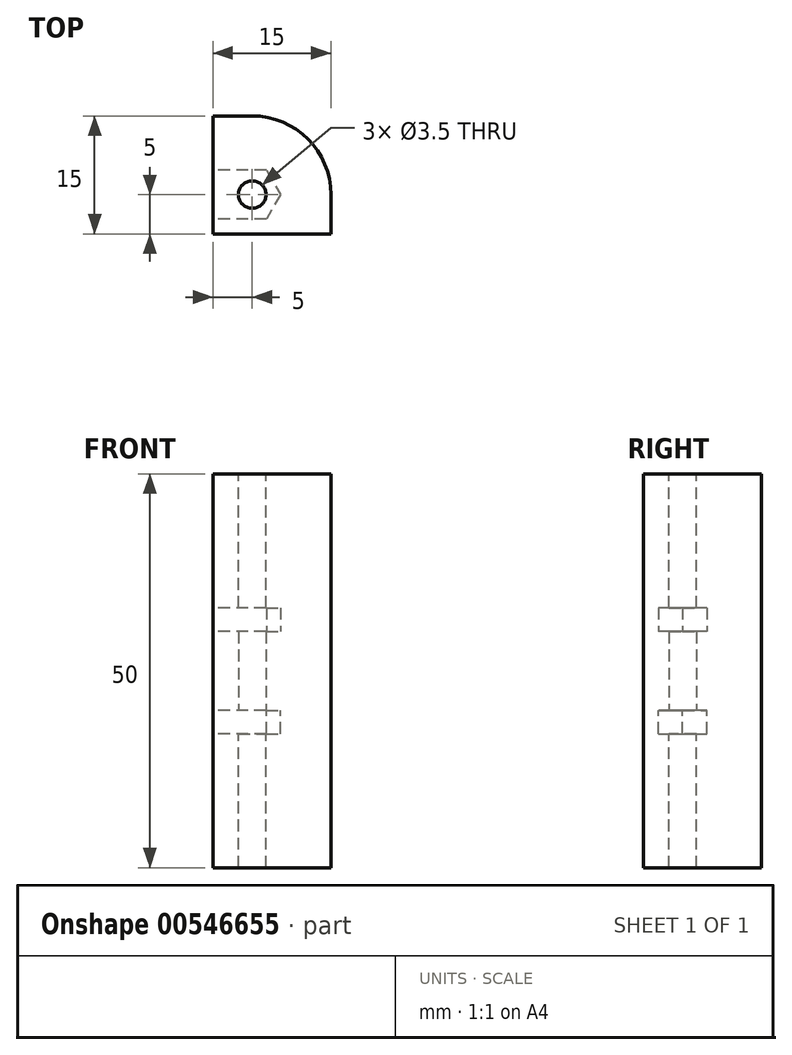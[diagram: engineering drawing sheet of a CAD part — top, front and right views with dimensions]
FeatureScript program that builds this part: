
annotation { "Feature Type Name" : "Feature", "Feature Type Description" : "" }
export const myFeature = defineFeature(function(context is Context, id is Id, definition is map)
    precondition{}
    {
        {
            var Q0;
            Q0=qCreatedBy(makeId("Top.planeOp"),FACE);
            var sketch = newSketch(context, id + "F0", { "sketchPlane" : qUnion([Q0])});
            skLineSegment(sketch, "E0.bottom", {"start": v(-2.5, 7.5) * mm, "end": v(-7.5, 7.5) * mm});
            skLineSegment(sketch, "E0.top", {"start": v(7.5, -7.5) * mm, "end": v(-7.5, -7.5) * mm});
            skLineSegment(sketch, "E0.left", {"start": v(7.5, -2.5) * mm, "end": v(7.5, -7.5) * mm});
            skLineSegment(sketch, "E0.right", {"start": v(-7.5, 7.5) * mm, "end": v(-7.5, -7.5) * mm});
            skPoint(sketch, "E0.middle", {"position": v(0, 0) * mm});
            skPoint(sketch, "E1.visualSharp", {"position": v(7.5, 7.5) * mm});
            skArc(sketch, "E1.filletArc", {"start": v(7.5, -2.5) * mm, "mid": v(4.57, 4.57) * mm, "end": v(-2.5, 7.5) * mm});
            skCircle(sketch, "E2", {"center": v(-2.5, -2.5) * mm, "radius": 1.75 * mm});
            skSolve(sketch);
        }
        {
            var Q0;
            Q0=makeQuery(id+"F0.imprint","IMPRINT",FACE,{"disambiguationData":[TD([[makeQuery(id+"F0.imprint","IMPRINT",EDGE,{"derivedFrom":sQuery(id+"F0.wireOp",EDGE,"E0.bottom")}),1.0]])]});
            extrude(context, id + "F1", {"entities" : qUnion([Q0]), "endBound" : BoundingType.SYMMETRIC, "depth" : 10 * mm, "offsetDistance" : 25 * mm});
        }
        {
            var Q0;
            Q0=makeQuery(id+"F1.opExtrude","CAP_FACE",FACE,{"disambiguationData":[OSD([sQuery(id+"F0.wireOp",EDGE,"E0.bottom"),sQuery(id+"F0.wireOp",EDGE,"E0.top"),sQuery(id+"F0.wireOp",EDGE,"E0.left"),sQuery(id+"F0.wireOp",EDGE,"E0.right"),sQuery(id+"F0.wireOp",EDGE,"E1.filletArc"),sQuery(id+"F0.wireOp",EDGE,"E2")])],"isStart":false});
            var sketch = newSketch(context, id + "F2", { "sketchPlane" : qUnion([Q0])});
            skLineSegment(sketch, "E3.0", {"start": v(-4.29, 0.6) * mm, "end": v(-0.71, 0.6) * mm});
            skLineSegment(sketch, "E3.1", {"start": v(-0.71, 0.6) * mm, "end": v(1.08, -2.5) * mm});
            skLineSegment(sketch, "E3.2", {"start": v(1.08, -2.5) * mm, "end": v(-0.71, -5.6) * mm});
            skLineSegment(sketch, "E3.3", {"start": v(-0.71, -5.6) * mm, "end": v(-4.29, -5.6) * mm});
            skPoint(sketch, "E3.0.midPoint", {"position": v(-2.5, 0.6) * mm});
            skLineSegment(sketch, "E4", {"start": v(-4.29, 0.6) * mm, "end": v(-7.5, 0.6) * mm});
            skLineSegment(sketch, "E5", {"start": v(-4.29, -5.6) * mm, "end": v(-7.5, -5.6) * mm});
            skSolve(sketch);
        }
        {
            var Q0;
            Q0=makeQuery(id+"F2.imprint","IMPRINT",FACE,{"disambiguationData":[TD([[makeQuery(id+"F2.imprint","IMPRINT",EDGE,{"derivedFrom":sQuery(id+"F2.wireOp",EDGE,"E3.0")}),1.0]])]});
            extrude(context, id + "F3", {"entities" : qUnion([Q0]), "operationType" : NewBodyOperationType.ADD, "depth" : 3 * mm, "offsetDistance" : 25 * mm});
        }
        {
            var Q0;
            Q0=makeQuery(id+"F1.opExtrude","CAP_FACE",FACE,{"disambiguationData":[OSD([sQuery(id+"F0.wireOp",EDGE,"E0.bottom"),sQuery(id+"F0.wireOp",EDGE,"E0.top"),sQuery(id+"F0.wireOp",EDGE,"E0.left"),sQuery(id+"F0.wireOp",EDGE,"E0.right"),sQuery(id+"F0.wireOp",EDGE,"E1.filletArc"),sQuery(id+"F0.wireOp",EDGE,"E2")])],"isStart":true});
            var sketch = newSketch(context, id + "F4", { "sketchPlane" : qUnion([Q0])});
            skLineSegment(sketch, "E6.0", {"start": v(-0.71, -0.6) * mm, "end": v(-4.29, -0.6) * mm});
            skLineSegment(sketch, "E6.3", {"start": v(-4.29, 5.6) * mm, "end": v(-0.71, 5.6) * mm});
            skLineSegment(sketch, "E6.4", {"start": v(-0.71, 5.6) * mm, "end": v(1.08, 2.5) * mm});
            skLineSegment(sketch, "E6.5", {"start": v(1.08, 2.5) * mm, "end": v(-0.71, -0.6) * mm});
            skPoint(sketch, "E6.0.midPoint", {"position": v(-2.5, -0.6) * mm});
            skLineSegment(sketch, "E7", {"start": v(-4.29, 5.6) * mm, "end": v(-7.5, 5.6) * mm});
            skLineSegment(sketch, "E8", {"start": v(-4.29, -0.6) * mm, "end": v(-7.5, -0.6) * mm});
            skSolve(sketch);
        }
        {
            var Q0;
            Q0 = qSketchRegion(id + "F4", true);
            var Q1;
            Q1=makeQuery(id+"F4.imprint","IMPRINT",FACE,{"disambiguationData":[TD([[makeQuery(id+"F4.imprint","IMPRINT",EDGE,{"derivedFrom":sQuery(id+"F4.wireOp",EDGE,"E6.0")}),1.0]])]});
            extrude(context, id + "F5", {"entities" : qUnion([Q0, Q1]), "operationType" : NewBodyOperationType.ADD, "depth" : 3 * mm, "offsetDistance" : 25 * mm});
        }
        {
            var Q0;
            Q0=makeQuery(id+"F3.opExtrude","CAP_FACE",FACE,{"disambiguationData":[OSD([sQuery(id+"F0.wireOp",EDGE,"E0.bottom"),sQuery(id+"F0.wireOp",EDGE,"E0.top"),sQuery(id+"F0.wireOp",EDGE,"E0.left"),sQuery(id+"F0.wireOp",EDGE,"E0.right"),sQuery(id+"F0.wireOp",EDGE,"E1.filletArc"),sQuery(id+"F2.wireOp",EDGE,"E3.0"),sQuery(id+"F2.wireOp",EDGE,"E3.1"),sQuery(id+"F2.wireOp",EDGE,"E3.2"),sQuery(id+"F2.wireOp",EDGE,"E3.3"),sQuery(id+"F2.wireOp",EDGE,"E4"),sQuery(id+"F2.wireOp",EDGE,"E5")])],"isStart":false});
            var sketch = newSketch(context, id + "F6", { "sketchPlane" : qUnion([Q0])});
            skLineSegment(sketch, "E9.bottom", {"start": v(-7.5, -7.5) * mm, "end": v(7.5, -7.5) * mm});
            skLineSegment(sketch, "E9.top", {"start": v(-7.5, 7.5) * mm, "end": v(-2.5, 7.5) * mm});
            skLineSegment(sketch, "E9.left", {"start": v(-7.5, -7.5) * mm, "end": v(-7.5, 7.5) * mm});
            skLineSegment(sketch, "E9.right", {"start": v(7.5, -7.5) * mm, "end": v(7.5, -2.5) * mm});
            skPoint(sketch, "E9.middle", {"position": v(0, 0) * mm});
            skPoint(sketch, "E10.visualSharp", {"position": v(7.5, 7.5) * mm});
            skArc(sketch, "E10.filletArc", {"start": v(7.5, -2.5) * mm, "mid": v(4.57, 4.57) * mm, "end": v(-2.5, 7.5) * mm});
            skSolve(sketch);
        }
        {
            var Q0;
            Q0 = qSketchRegion(id + "F6", true);
            extrude(context, id + "F7", {"entities" : qUnion([Q0]), "operationType" : NewBodyOperationType.ADD, "depth" : 17 * mm, "offsetDistance" : 25 * mm});
        }
        {
            var Q0;
            Q0=makeQuery(id+"F5.opExtrude","CAP_FACE",FACE,{"disambiguationData":[OSD([sQuery(id+"F0.wireOp",EDGE,"E0.bottom"),sQuery(id+"F0.wireOp",EDGE,"E0.top"),sQuery(id+"F0.wireOp",EDGE,"E0.left"),sQuery(id+"F0.wireOp",EDGE,"E0.right"),sQuery(id+"F0.wireOp",EDGE,"E1.filletArc"),sQuery(id+"F4.wireOp",EDGE,"E6.0"),sQuery(id+"F4.wireOp",EDGE,"E6.3"),sQuery(id+"F4.wireOp",EDGE,"E6.4"),sQuery(id+"F4.wireOp",EDGE,"E6.5"),sQuery(id+"F4.wireOp",EDGE,"E7"),sQuery(id+"F4.wireOp",EDGE,"E8")])],"isStart":false});
            var sketch = newSketch(context, id + "F8", { "sketchPlane" : qUnion([Q0])});
            skLineSegment(sketch, "E11.bottom", {"start": v(-7.5, 7.5) * mm, "end": v(7.5, 7.5) * mm});
            skLineSegment(sketch, "E11.top", {"start": v(-7.5, -7.5) * mm, "end": v(-2.5, -7.5) * mm});
            skLineSegment(sketch, "E11.left", {"start": v(-7.5, 7.5) * mm, "end": v(-7.5, -7.5) * mm});
            skLineSegment(sketch, "E11.right", {"start": v(7.5, 7.5) * mm, "end": v(7.5, 2.5) * mm});
            skPoint(sketch, "E11.middle", {"position": v(0, 0) * mm});
            skPoint(sketch, "E12.visualSharp", {"position": v(7.5, -7.5) * mm});
            skArc(sketch, "E12.filletArc", {"start": v(-2.5, -7.5) * mm, "mid": v(4.57, -4.57) * mm, "end": v(7.5, 2.5) * mm});
            skCircle(sketch, "E13", {"center": v(-2.5, 2.5) * mm, "radius": 1.75 * mm});
            skSolve(sketch);
        }
        {
            var Q0;
            Q0=makeQuery(id+"F8.imprint","IMPRINT",FACE,{"disambiguationData":[TD([[makeQuery(id+"F8.imprint","IMPRINT",EDGE,{"derivedFrom":sQuery(id+"F8.wireOp",EDGE,"E13")}),-1.0]])]});
            var Q1;
            {var subQ1=sQuery(id+"F8.wireOp",EDGE,"E11.bottom");Q1=makeQuery(id+"F8.imprint","IMPRINT",FACE,{"disambiguationData":[TD([[makeQuery(id+"F8.imprint","IMPRINT",EDGE,{"derivedFrom":subQ1}),1.0]])]});}
            extrude(context, id + "F9", {"entities" : qUnion([Q0, Q1]), "operationType" : NewBodyOperationType.ADD, "depth" : 17 * mm, "offsetDistance" : 25 * mm});
        }
        {
            var Q0;
            Q0=makeQuery(id+"F7.opExtrude","CAP_FACE",FACE,{"disambiguationData":[OSD([sQuery(id+"F6.wireOp",EDGE,"E9.bottom"),sQuery(id+"F6.wireOp",EDGE,"E9.top"),sQuery(id+"F6.wireOp",EDGE,"E9.left"),sQuery(id+"F6.wireOp",EDGE,"E9.right"),sQuery(id+"F6.wireOp",EDGE,"E10.filletArc")])],"isStart":false});
            var sketch = newSketch(context, id + "F10", { "sketchPlane" : qUnion([Q0])});
            skCircle(sketch, "E14", {"center": v(-2.5, -2.5) * mm, "radius": 1.75 * mm});
            skSolve(sketch);
        }
        {
            var Q0;
            Q0=makeQuery(id+"F10.imprint","IMPRINT",FACE,{"disambiguationData":[TD([[makeQuery(id+"F10.imprint","IMPRINT",EDGE,{"derivedFrom":sQuery(id+"F10.wireOp",EDGE,"E14")}),1.0]])]});
            var Q1;
            Q1=sQuery(id+"F10.wireOp",EDGE,"E14");
            extrude(context, id + "F11", {"entities" : qUnion([Q0]), "operationType" : NewBodyOperationType.REMOVE, "surfaceEntities" : qUnion([Q1]), "oppositeDirection" : true, "depth" : 50 * mm, "offsetDistance" : 25 * mm});
        }
    });
